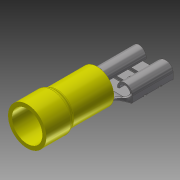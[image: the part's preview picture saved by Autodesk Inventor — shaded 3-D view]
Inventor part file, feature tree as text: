
AUTODESK INVENTOR PART (.ipt)
format: ipt  version: 2014 (Build 180170000, 170)  size: 521,216 bytes
history: native  units: in
note: dims shown in document units (in); Inventor stores cm internally (conversion verified against a paired STEP export)
features: sketch x13, extrude x10, projected_geometry x9, fillet x5, plane x3, shell x1, revolve x1, mirror x1, loft x1, chamfer x1
ambient origin geometry x8: Origin, YZ Plane, XZ Plane, XY Plane, X Axis, Y Axis, Z Axis, Center Point
bodies: Solid1 (feature_tree), Solid2 (feature_tree)
feature tree (45):
  extrude  "Extrusion1"  Depth=0.5in TaperAngle=0.0deg
  extrude  "Extrusion2"  Depth=0.03in TaperAngle=0.0deg
  fillet  "Fillet1"  Radius=0.02in
  fillet  "Fillet2"  Radius=0.03in
  shell  "Shell1"  Thickness=0.026in
  revolve  "Revolution1"  Angle=90.0deg
  plane  "Work Plane1"
  plane  "Work Plane2"
  extrude  "Extrusion3"  Depth=0.2905in
  mirror  "Mirror1"
  loft  "Loft2"
  fillet  "Fillet3"  Radius=0.109in
  chamfer  "Chamfer1"  Distance=0.291in
  extrude  "Extrusion4"  Depth=0.03in TaperAngle=45.0deg
  extrude  "Extrusion5"  Depth=0.3937in TaperAngle=90.0deg
  fillet  "Fillet4"  Radius=0.015in
  extrude  "Extrusion6"  Depth=0.015in TaperAngle=0.0deg
  extrude  "Extrusion7"  Depth=0.005in
  extrude  "Extrusion8"  Depth=0.003in TaperAngle=0.0deg
  fillet  "Fillet5"  Radius=0.003in
  plane  "Work Plane3"
  extrude  "Extrusion9"  Depth=0.005in
  extrude  "Extrusion10"  Depth=0.005in
  sketch  "Sketch1"  dims[d0=0.2415in d1=0.5in d2=0.0in]
  sketch  "Sketch2"  dims[d3=0.2715in d4=0.195in d5=0.0in d6=0.02in d7=0.03in d8=0.026in]
  projected_geometry  "Projected Loop1"
  sketch  "Sketch3"  dims[d9=0.014in d10=90.0deg]
  sketch  "Sketch5"  dims[d11=0.4in d12=0.2905in]
  sketch  "Sketch6"  dims[d13=0.0135in d14=0.037in d15=0.109in]
  projected_geometry  "Projected Loop2"
  sketch  "Sketch7"  dims[d16=0.01in d17=0.291in d18=0.0in]
  projected_geometry  "Projected Loop3"
  sketch  "Sketch8"  dims[d23=0.03in d24=0.003in d25=0.125in d26=45.0deg]
  projected_geometry  "Projected Loop4"
  sketch  "Sketch9"  dims[d27=0.0in d28=90.0deg d29=0.3937in d30=90.0deg d31=0.015in]
  projected_geometry  "Projected Loop5"
  sketch  "Sketch10"  dims[d32=0.291in d33=0.0in d34=0.015in d35=0.0in]
  projected_geometry  "Projected Loop6"
  sketch  "Sketch11"  dims[d36=0.005in d37=0.0235in]
  projected_geometry  "Projected Loop7"
  sketch  "Sketch12"  dims[d38=0.014in d39=0.0in d40=0.003in d41=0.0in d42=0.003in d43=0.0in]
  sketch  "Sketch14"  dims[d44=0.005in d45=0.01in]
  sketch  "Sketch15"  dims[d46=0.003in d47=0.0in d48=0.005in d49=0.05in d50=0.0in]
  projected_geometry  "Projected Loop8"
  projected_geometry  "Project Cut Edges1"
